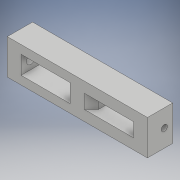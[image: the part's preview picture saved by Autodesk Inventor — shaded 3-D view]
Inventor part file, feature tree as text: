
AUTODESK INVENTOR PART (.ipt)
format: ipt  version: 2017 (Build 210142000, 142)  size: 128,000 bytes
history: native  units: mm
features: sketch x2, hole x2, extrude x1, other x1, chamfer x1
ambient origin geometry x8: Origin, YZ Plane, XZ Plane, XY Plane, X Axis, Y Axis, Z Axis, Center Point
bodies: Solid1 (feature_tree)
feature tree (7):
  extrude  "Extrusion1"  Depth=25.0mm
  other  "M6 thru"
  sketch  "Sketch3"  dims[d2=10.0mm d3=13.0mm d4=18.0mm d5=0.0mm d6=6.4mm d7=6.0mm d8=4.0mm d9=2.0mm d10=90.0deg d11=8.0mm d12=0.0mm d13=7.0mm d14=12.0mm d15=4.4mm d16=6.0mm d17=4.0mm d18=2.0mm d19=90.0deg d20=8.0mm d21=0.0mm d22=5.0mm d23=2.0mm d24=45.0deg]
  hole  "M6 thru-hole"  [1 undecoded]
  hole  "M4 thru-hole"  [1 undecoded]
  chamfer  "Chamfer1"  Distance=7.0mm
  sketch  "Sketch1"  dims[d0=100.0mm d1=25.0mm]
note: 2 required parameter values undecoded (feature->parameter linkage not recoverable at this tier; creation-order binding heuristic only, values carry confidence <= 0.55)
